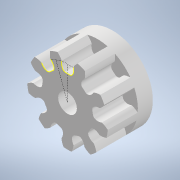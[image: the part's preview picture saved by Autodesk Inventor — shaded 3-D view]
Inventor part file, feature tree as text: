
AUTODESK INVENTOR PART (.ipt)
format: ipt  version: 2022 (Build 260153070, 153G)  size: 410,624 bytes
history: native  units: mm
features: extrude x5, sketch x4, pattern_circular x1
ambient origin geometry x8: Origin, YZ Plane, XZ Plane, XY Plane, X Axis, Y Axis, Z Axis, Center Point
bodies: Solid1 (feature_tree)
feature tree (10):
  sketch  "Sketch1"  dims[d0=3.0mm d1=0.0mm]
  extrude  "Extrusion1"  TaperAngle=0.0deg  [1 undecoded]
  extrude  "Extrusion2"  Depth=90.0mm TaperAngle=360.0deg
  pattern_circular  "Circular Pattern1"  [2 undecoded]
  sketch  "Sketch2"  dims[d2=10.0mm d3=0.0mm d4=90.0mm d5=360.0deg]
  extrude  "Extrusion3"  Depth=6.1mm
  extrude  "Extrusion4"  Depth=2.0mm TaperAngle=0.0deg
  extrude  "Extrusion5"  [1 undecoded]
  sketch  "Sketch3"  dims[d7=2.5mm]
  sketch  "Sketch5"  dims[d8=3.0mm d9=0.0mm d10=1.0mm d11=0.0mm d12=6.1mm d14=2.0mm d15=0.0mm]
note: 4 required parameter values undecoded (feature->parameter linkage not recoverable at this tier; creation-order binding heuristic only, values carry confidence <= 0.55)
